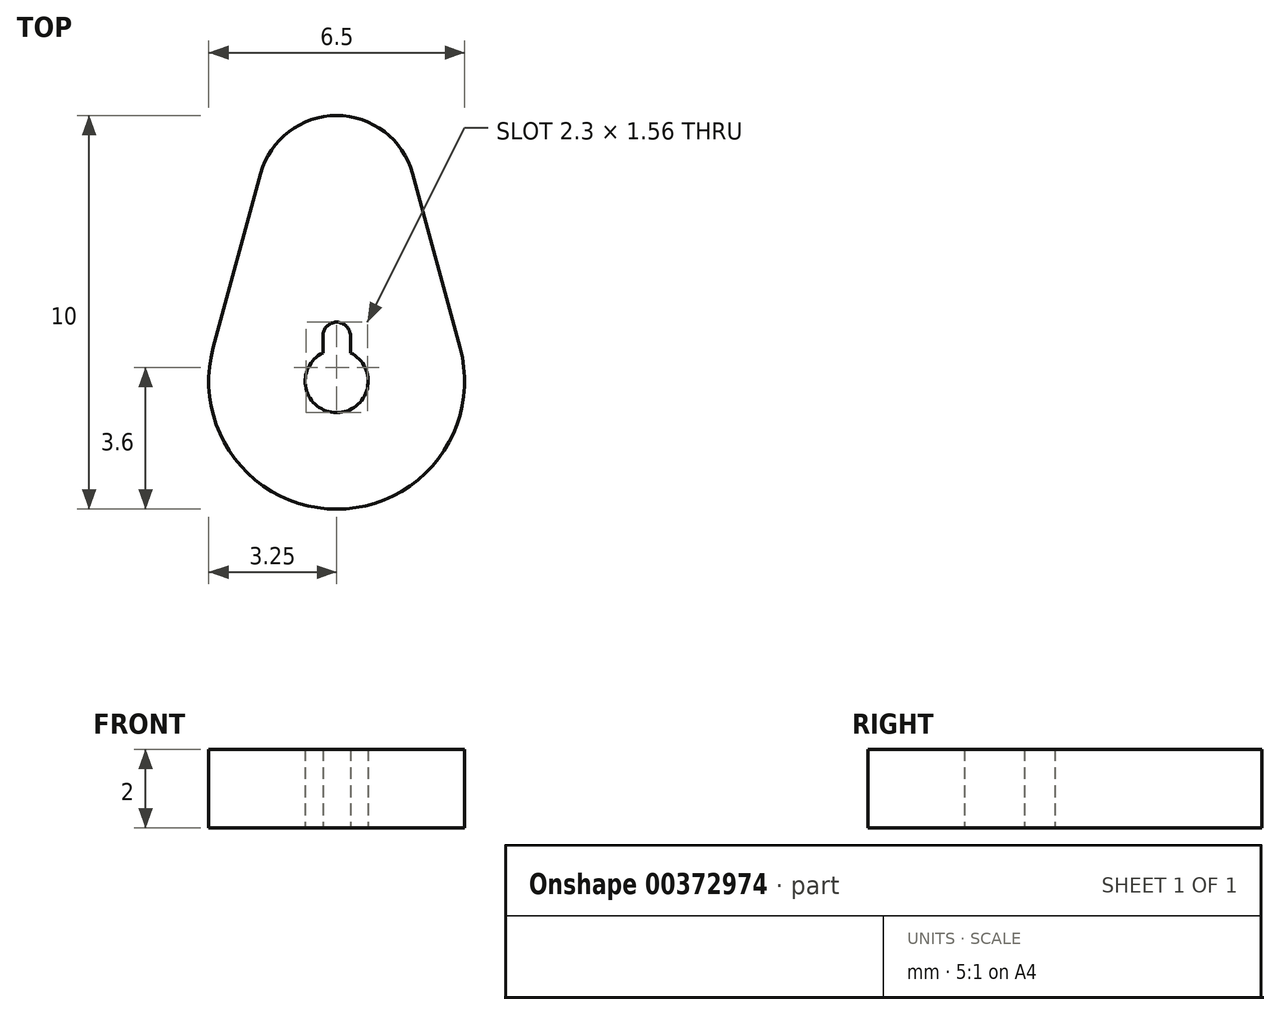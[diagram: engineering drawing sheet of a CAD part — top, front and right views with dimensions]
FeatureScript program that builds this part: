
annotation { "Feature Type Name" : "Feature", "Feature Type Description" : "" }
export const myFeature = defineFeature(function(context is Context, id is Id, definition is map)
    precondition{}
    {
        {
            var Q0;
            Q0=qCreatedBy(makeId("Top.planeOp"),FACE);
            var sketch = newSketch(context, id + "F0", { "sketchPlane" : qUnion([Q0])});
            skCircle(sketch, "E0", {"center": v(0, 0) * mm, "radius": 6.75 * mm, "construction": true});
            skCircle(sketch, "E1", {"center": v(0, 0) * mm, "radius": 3.25 * mm, "construction": true});
            skArc(sketch, "E2", {"start": v(0, 6.75) * mm, "mid": v(-1.21, 6.34) * mm, "end": v(-1.93, 5.28) * mm});
            skLineSegment(sketch, "E3", {"start": v(-1.93, 5.28) * mm, "end": v(-3.14, 0.86) * mm});
            skLineSegment(sketch, "E4", {"start": v(0, -8.78) * mm, "end": v(0, 0) * mm, "construction": true});
            skArc(sketch, "E5", {"start": v(-3.14, 0.86) * mm, "mid": v(-2.58, -1.97) * mm, "end": v(0, -3.25) * mm});
            skLineSegment(sketch, "E6", {"start": v(0, 0) * mm, "end": v(0, 7.69) * mm, "construction": true});
            skArc(sketch, "E7.MirrorCS", {"start": v(3.14, 0.86) * mm, "mid": v(2.58, -1.97) * mm, "end": v(0, -3.25) * mm});
            skLineSegment(sketch, "E8.MirrorCS", {"start": v(1.93, 5.28) * mm, "end": v(3.14, 0.86) * mm});
            skArc(sketch, "E9.MirrorCS", {"start": v(0, 6.75) * mm, "mid": v(1.21, 6.34) * mm, "end": v(1.93, 5.28) * mm});
            skArc(sketch, "E10", {"start": v(-0.35, 0.72) * mm, "mid": v(0, -0.8) * mm, "end": v(0.35, 0.72) * mm});
            skCircle(sketch, "E11", {"center": v(0, 0) * mm, "radius": 1.5 * mm, "construction": true});
            skArc(sketch, "E12", {"start": v(0.35, 1.15) * mm, "mid": v(0, 1.5) * mm, "end": v(-0.35, 1.15) * mm});
            skLineSegment(sketch, "E13", {"start": v(-0.35, 1.15) * mm, "end": v(-0.35, 0.72) * mm});
            skLineSegment(sketch, "E14", {"start": v(0.35, 1.15) * mm, "end": v(0.35, 0.72) * mm});
            skSolve(sketch);
        }
        {
            var Q0;
            Q0 = qSketchRegion(id + "F0", true);
            extrude(context, id + "F1", {"entities" : qUnion([Q0]), "depth" : 2 * mm, "offsetDistance" : 25 * mm});
        }
    });
